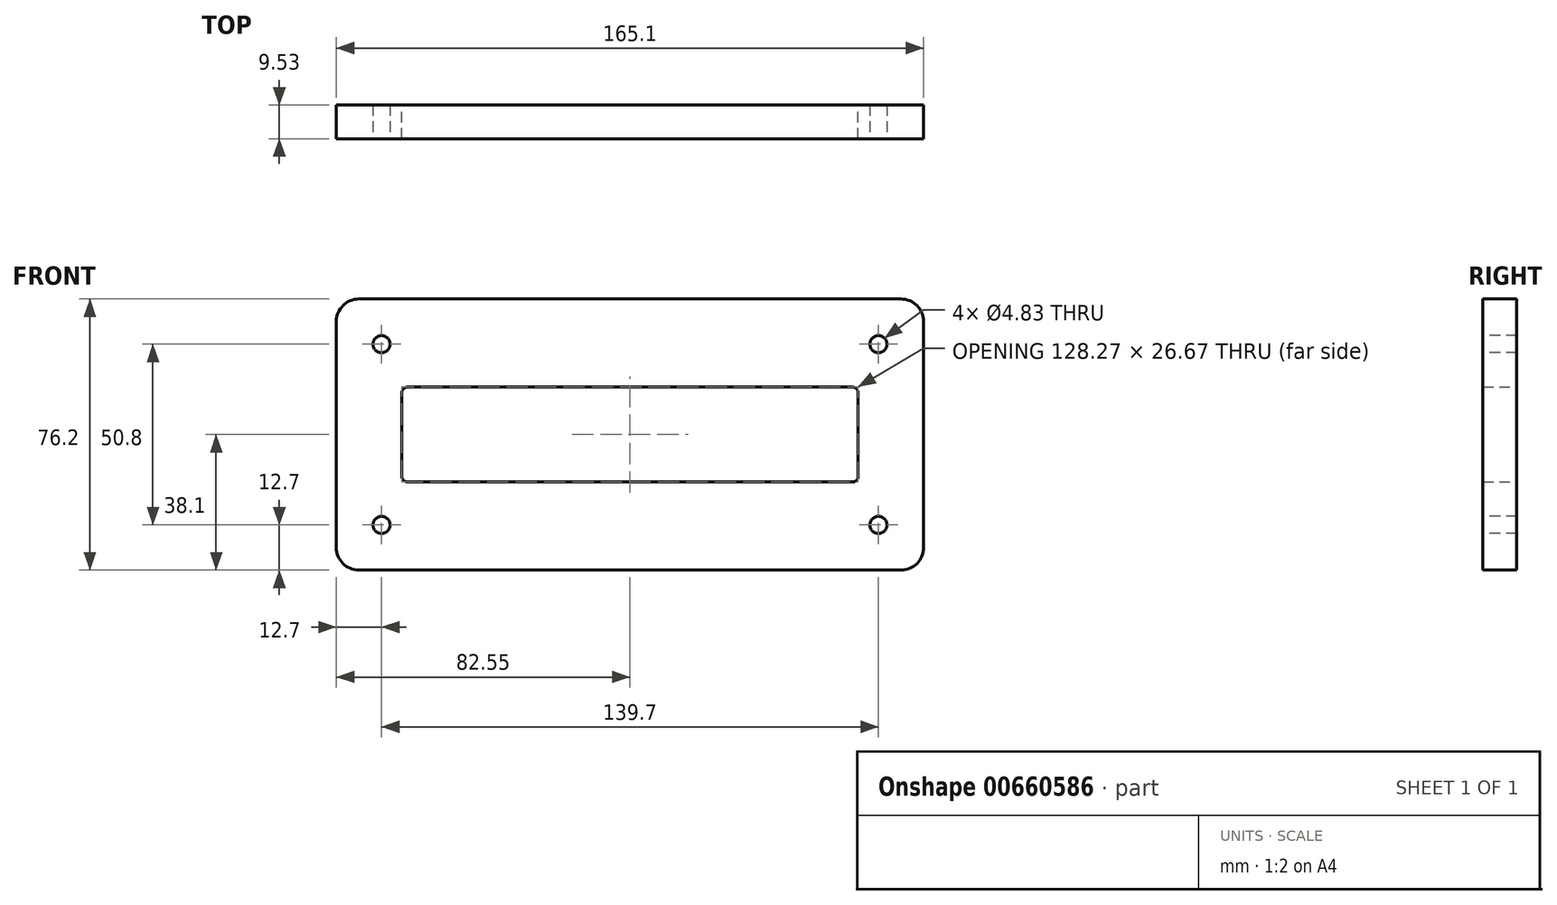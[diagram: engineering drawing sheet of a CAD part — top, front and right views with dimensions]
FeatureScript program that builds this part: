
annotation { "Feature Type Name" : "Feature", "Feature Type Description" : "" }
export const myFeature = defineFeature(function(context is Context, id is Id, definition is map)
    precondition{}
    {
        {
            var Q0;
            Q0=qCreatedBy(makeId("Front.planeOp"),FACE);
            var sketch = newSketch(context, id + "F0", { "sketchPlane" : qUnion([Q0])});
            skLineSegment(sketch, "E0.bottom", {"start": v(82.55, 38.1) * mm, "end": v(-82.55, 38.1) * mm});
            skLineSegment(sketch, "E0.top", {"start": v(82.55, -38.1) * mm, "end": v(-82.55, -38.1) * mm});
            skLineSegment(sketch, "E0.left", {"start": v(82.55, 38.1) * mm, "end": v(82.55, -38.1) * mm});
            skLineSegment(sketch, "E0.right", {"start": v(-82.55, 38.1) * mm, "end": v(-82.55, -38.1) * mm});
            skPoint(sketch, "E0.middle", {"position": v(0, 0) * mm});
            skLineSegment(sketch, "E1.bottom", {"start": v(64.13, 13.34) * mm, "end": v(-64.13, 13.34) * mm});
            skLineSegment(sketch, "E1.top", {"start": v(64.14, -13.34) * mm, "end": v(-64.13, -13.34) * mm});
            skLineSegment(sketch, "E1.left", {"start": v(64.13, 13.34) * mm, "end": v(64.14, -13.34) * mm});
            skLineSegment(sketch, "E1.right", {"start": v(-64.14, 13.34) * mm, "end": v(-64.13, -13.34) * mm});
            skSolve(sketch);
        }
        {
            var Q0;
            Q0=makeQuery(id+"F0.imprint","IMPRINT",FACE,{"disambiguationData":[TD([[makeQuery(id+"F0.imprint","IMPRINT",EDGE,{"derivedFrom":sQuery(id+"F0.wireOp",EDGE,"E0.bottom")}),1.0]])]});
            extrude(context, id + "F1", {"entities" : qUnion([Q0]), "depth" : 9.52 * mm, "offsetDistance" : 25.4 * mm});
        }
        {
            var Q0;
            Q0=makeQuery(id+"F1.opExtrude","CAP_FACE",FACE,{"disambiguationData":[OSD([sQuery(id+"F0.wireOp",EDGE,"E0.bottom"),sQuery(id+"F0.wireOp",EDGE,"E0.top"),sQuery(id+"F0.wireOp",EDGE,"E0.left"),sQuery(id+"F0.wireOp",EDGE,"E0.right"),sQuery(id+"F0.wireOp",EDGE,"E1.bottom"),sQuery(id+"F0.wireOp",EDGE,"E1.top"),sQuery(id+"F0.wireOp",EDGE,"E1.left"),sQuery(id+"F0.wireOp",EDGE,"E1.right")])],"isStart":false});
            var sketch = newSketch(context, id + "F2", { "sketchPlane" : qUnion([Q0])});
            skPoint(sketch, "E2", {"position": v(-69.85, 25.4) * mm});
            skPoint(sketch, "E3", {"position": v(69.85, 25.4) * mm});
            skPoint(sketch, "E4", {"position": v(69.85, -25.4) * mm});
            skPoint(sketch, "E5", {"position": v(-69.85, -25.4) * mm});
            skSolve(sketch);
        }
        {
            var Q0;
            Q0=sQuery(id+"F2.wireOp",VERTEX,"E2");
            var Q1;
            Q1=sQuery(id+"F2.wireOp",VERTEX,"E3");
            var Q2;
            Q2=sQuery(id+"F2.wireOp",VERTEX,"E4");
            var Q3;
            Q3=sQuery(id+"F2.wireOp",VERTEX,"E5");
            var Q4;
            Q4=makeQuery(id+"F1.opExtrude","SWEPT_BODY",BODY,{"disambiguationData":[OSD([sQuery(id+"F0.wireOp",EDGE,"E0.bottom"),sQuery(id+"F0.wireOp",EDGE,"E0.top"),sQuery(id+"F0.wireOp",EDGE,"E0.left"),sQuery(id+"F0.wireOp",EDGE,"E0.right"),sQuery(id+"F0.wireOp",EDGE,"E1.bottom"),sQuery(id+"F0.wireOp",EDGE,"E1.top"),sQuery(id+"F0.wireOp",EDGE,"E1.left"),sQuery(id+"F0.wireOp",EDGE,"E1.right")])]});
            hole(context, id + "F3", {"style" : HoleStyle.SIMPLE, "endStyle" : HoleEndStyle.THROUGH, "holeDiameter" : 4.83 * mm, "majorDiameter" : 6.35 * mm, "isTappedThrough" : true, "tappedDepth" : 12.7 * mm, "tapClearance" : 3, "startFromSketch" : true, "locations" : qUnion([Q0, Q1, Q2, Q3]), "scope" : qUnion([Q4])});
        }
        {
            var Q0;
            Q0=makeQuery(id+"F1.opExtrude","SWEPT_EDGE",EDGE,{"disambiguationData":[OSD([sQuery(id+"F0.wireOp",EDGE,"E1.bottom"),sQuery(id+"F0.wireOp",EDGE,"E1.right")])]});
            var Q1;
            Q1=makeQuery(id+"F1.opExtrude","SWEPT_EDGE",EDGE,{"disambiguationData":[OSD([sQuery(id+"F0.wireOp",EDGE,"E1.top"),sQuery(id+"F0.wireOp",EDGE,"E1.right")])]});
            var Q2;
            Q2=makeQuery(id+"F1.opExtrude","SWEPT_EDGE",EDGE,{"disambiguationData":[OSD([sQuery(id+"F0.wireOp",EDGE,"E1.top"),sQuery(id+"F0.wireOp",EDGE,"E1.left")])]});
            var Q3;
            Q3=makeQuery(id+"F1.opExtrude","SWEPT_EDGE",EDGE,{"disambiguationData":[OSD([sQuery(id+"F0.wireOp",EDGE,"E1.bottom"),sQuery(id+"F0.wireOp",EDGE,"E1.left")])]});
            fillet(context, id + "F4", {"entities" : qUnion([Q0, Q1, Q2, Q3]), "radius" : 1.59 * mm, "tangentPropagation" : true, "allowEdgeOverflow" : false});
        }
        {
            var Q0;
            Q0=makeQuery(id+"F1.opExtrude","SWEPT_EDGE",EDGE,{"disambiguationData":[OSD([sQuery(id+"F0.wireOp",EDGE,"E0.bottom"),sQuery(id+"F0.wireOp",EDGE,"E0.left")])]});
            var Q1;
            Q1=makeQuery(id+"F1.opExtrude","SWEPT_EDGE",EDGE,{"disambiguationData":[OSD([sQuery(id+"F0.wireOp",EDGE,"E0.bottom"),sQuery(id+"F0.wireOp",EDGE,"E0.right")])]});
            var Q2;
            Q2=makeQuery(id+"F1.opExtrude","SWEPT_EDGE",EDGE,{"disambiguationData":[OSD([sQuery(id+"F0.wireOp",EDGE,"E0.top"),sQuery(id+"F0.wireOp",EDGE,"E0.left")])]});
            var Q3;
            Q3=makeQuery(id+"F1.opExtrude","SWEPT_EDGE",EDGE,{"disambiguationData":[OSD([sQuery(id+"F0.wireOp",EDGE,"E0.top"),sQuery(id+"F0.wireOp",EDGE,"E0.right")])]});
            fillet(context, id + "F5", {"entities" : qUnion([Q0, Q1, Q2, Q3]), "radius" : 6.35 * mm, "tangentPropagation" : true, "allowEdgeOverflow" : false});
        }
    });
